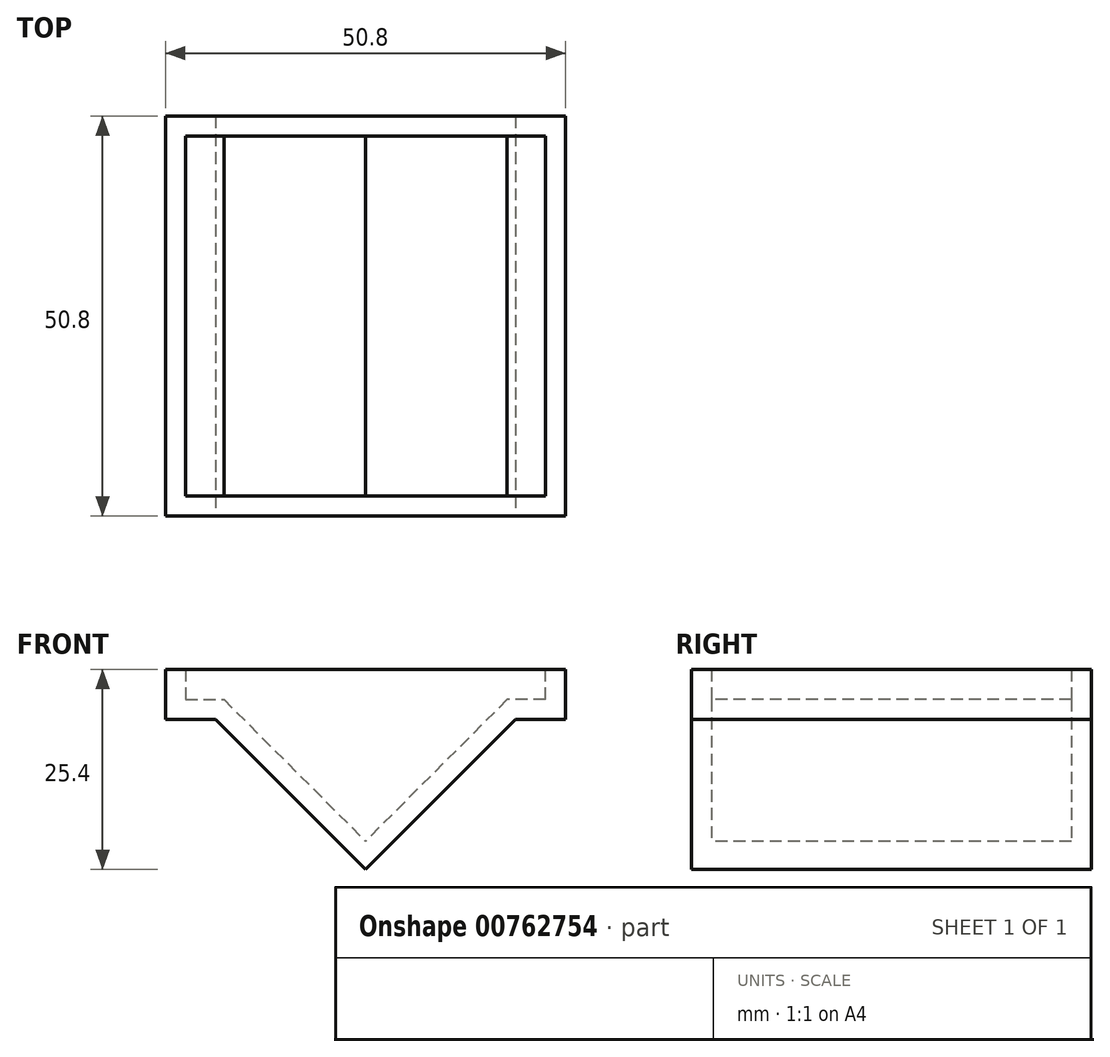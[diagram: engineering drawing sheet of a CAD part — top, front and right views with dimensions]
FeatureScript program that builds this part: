
annotation { "Feature Type Name" : "Feature", "Feature Type Description" : "" }
export const myFeature = defineFeature(function(context is Context, id is Id, definition is map)
    precondition{}
    {
        {
            var Q0;
            Q0=qCreatedBy(makeId("Front.planeOp"),FACE);
            var sketch = newSketch(context, id + "F0", { "sketchPlane" : qUnion([Q0])});
            skLineSegment(sketch, "E0", {"start": v(0, 0) * mm, "end": v(50.8, 0) * mm});
            skLineSegment(sketch, "E1", {"start": v(50.8, 0) * mm, "end": v(50.8, 25.4) * mm});
            skLineSegment(sketch, "E2", {"start": v(50.8, 25.4) * mm, "end": v(0, 25.4) * mm});
            skLineSegment(sketch, "E3", {"start": v(0, 25.4) * mm, "end": v(0, 0) * mm});
            skSolve(sketch);
        }
        {
            var Q0;
            Q0=makeQuery(id+"F0.imprint","IMPRINT",FACE,{"disambiguationData":[TD([[makeQuery(id+"F0.imprint","IMPRINT",EDGE,{"derivedFrom":sQuery(id+"F0.wireOp",EDGE,"E0")}),1.0]])]});
            extrude(context, id + "F1", {"entities" : qUnion([Q0]), "oppositeDirection" : true, "depth" : 50.8 * mm, "offsetDistance" : 25.4 * mm});
        }
        {
            var Q0;
            Q0=makeQuery(id+"F1.opExtrude","CAP_FACE",FACE,{"disambiguationData":[OSD([sQuery(id+"F0.wireOp",EDGE,"E0"),sQuery(id+"F0.wireOp",EDGE,"E1"),sQuery(id+"F0.wireOp",EDGE,"E2"),sQuery(id+"F0.wireOp",EDGE,"E3")])],"isStart":true});
            var sketch = newSketch(context, id + "F2", { "sketchPlane" : qUnion([Q0])});
            skLineSegment(sketch, "E4", {"start": v(0, 0) * mm, "end": v(0, 19.05) * mm});
            skLineSegment(sketch, "E5", {"start": v(0, 19.05) * mm, "end": v(6.35, 19.05) * mm});
            skLineSegment(sketch, "E6", {"start": v(6.35, 19.05) * mm, "end": v(25.4, 0) * mm});
            skLineSegment(sketch, "E7", {"start": v(25.4, 0) * mm, "end": v(44.46, 19.06) * mm});
            skLineSegment(sketch, "E8", {"start": v(44.46, 19.06) * mm, "end": v(50.8, 19.06) * mm});
            skLineSegment(sketch, "E9", {"start": v(50.8, 19.06) * mm, "end": v(50.8, 0) * mm});
            skLineSegment(sketch, "E10", {"start": v(50.8, 0) * mm, "end": v(0, 0) * mm});
            skSolve(sketch);
        }
        {
            var Q0;
            {var subQ0=sQuery(id+"F2.wireOp",EDGE,"E4");Q0=makeQuery(id+"F2.imprint","IMPRINT",FACE,{"disambiguationData":[TD([[makeQuery(id+"F2.imprint","IMPRINT",EDGE,{"derivedFrom":subQ0}),1.0]])]});}
            extrude(context, id + "F3", {"entities" : qUnion([Q0]), "operationType" : NewBodyOperationType.REMOVE, "oppositeDirection" : true, "depth" : 50.8 * mm, "offsetDistance" : 25.4 * mm});
        }
        {
            var Q0;
            Q0=makeQuery(id+"F1.opExtrude","CAP_FACE",FACE,{"disambiguationData":[OSD([sQuery(id+"F0.wireOp",EDGE,"E0"),sQuery(id+"F0.wireOp",EDGE,"E1"),sQuery(id+"F0.wireOp",EDGE,"E2"),sQuery(id+"F0.wireOp",EDGE,"E3")])],"isStart":true});
            var sketch = newSketch(context, id + "F4", { "sketchPlane" : qUnion([Q0])});
            skLineSegment(sketch, "E11", {"start": v(50.8, 0) * mm, "end": v(50.8, 19.05) * mm});
            skLineSegment(sketch, "E12", {"start": v(50.8, 19.05) * mm, "end": v(44.45, 19.05) * mm});
            skLineSegment(sketch, "E13", {"start": v(44.45, 19.05) * mm, "end": v(25.4, 0) * mm});
            skLineSegment(sketch, "E14", {"start": v(25.4, 0) * mm, "end": v(50.8, 0) * mm});
            skSolve(sketch);
        }
        {
            var Q0;
            Q0=makeQuery(id+"F4.imprint","IMPRINT",FACE,{"disambiguationData":[TD([[makeQuery(id+"F4.imprint","IMPRINT",EDGE,{"derivedFrom":sQuery(id+"F4.wireOp",EDGE,"E11")}),1.0]])]});
            extrude(context, id + "F5", {"entities" : qUnion([Q0]), "operationType" : NewBodyOperationType.REMOVE, "oppositeDirection" : true, "depth" : 50.8 * mm, "offsetDistance" : 25.4 * mm});
        }
        {
            var Q0;
            Q0=makeQuery(id+"F1.opExtrude","SWEPT_FACE",FACE,{"disambiguationData":[OSD([sQuery(id+"F0.wireOp",EDGE,"E2")])]});
            shell(context, id + "F6", {"entities" : qUnion([Q0]), "thickness" : 2.54 * mm});
        }
    });
